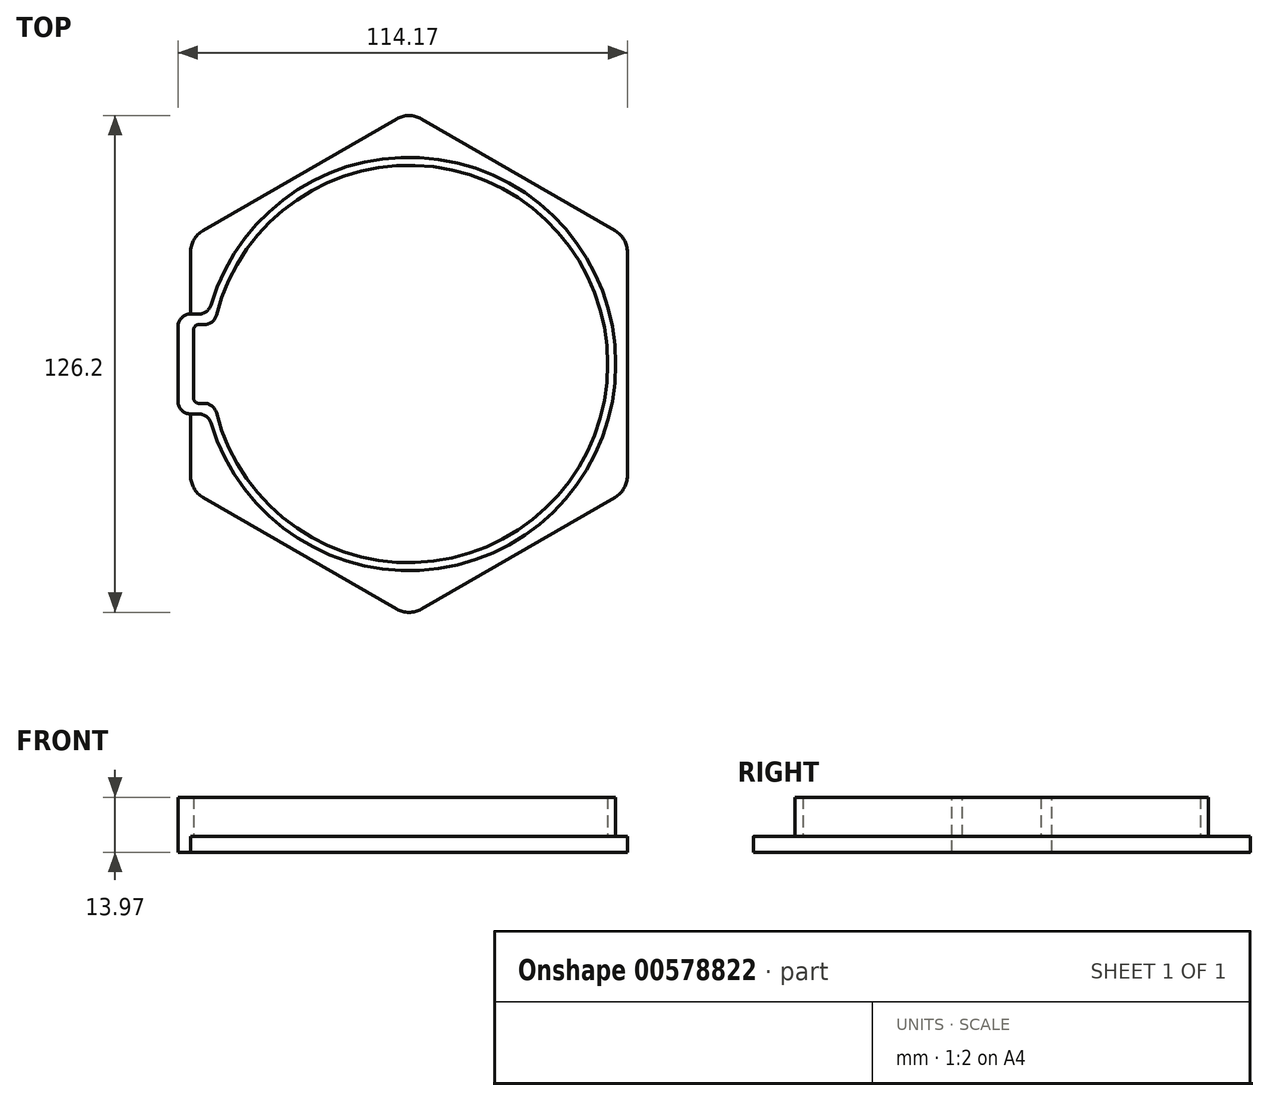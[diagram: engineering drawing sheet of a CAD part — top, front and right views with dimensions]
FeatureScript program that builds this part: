
annotation { "Feature Type Name" : "Feature", "Feature Type Description" : "" }
export const myFeature = defineFeature(function(context is Context, id is Id, definition is map)
    precondition{}
    {
        {
            var Q0;
            Q0=qCreatedBy(makeId("Top.planeOp"),FACE);
            var sketch = newSketch(context, id + "F0", { "sketchPlane" : qUnion([Q0])});
            skCircle(sketch, "E0.cCircle", {"center": v(0, 0) * mm, "radius": 64.08 * mm, "construction": true});
            skLineSegment(sketch, "E0.0", {"start": v(0, 64.08) * mm, "end": v(55.5, 32.04) * mm});
            skLineSegment(sketch, "E0.1", {"start": v(55.5, 32.04) * mm, "end": v(55.5, -32.04) * mm});
            skLineSegment(sketch, "E0.2", {"start": v(55.5, -32.04) * mm, "end": v(0, -64.08) * mm});
            skLineSegment(sketch, "E0.3", {"start": v(0, -64.08) * mm, "end": v(-55.5, -32.04) * mm});
            skLineSegment(sketch, "E0.4", {"start": v(-55.5, -32.04) * mm, "end": v(-55.5, 32.04) * mm});
            skLineSegment(sketch, "E0.5", {"start": v(-55.5, 32.04) * mm, "end": v(0, 64.08) * mm});
            skSolve(sketch);
        }
        {
            var Q0;
            Q0=makeQuery(id+"F0.imprint","IMPRINT",FACE,{"disambiguationData":[TD([[makeQuery(id+"F0.imprint","IMPRINT",EDGE,{"derivedFrom":sQuery(id+"F0.wireOp",EDGE,"E0.0")}),-1.0]])]});
            extrude(context, id + "F1", {"entities" : qUnion([Q0]), "depth" : 4 * mm, "offsetDistance" : 25.4 * mm});
        }
        {
            var Q0;
            Q0=makeQuery(id+"F1.opExtrude","CAP_FACE",FACE,{"disambiguationData":[OSD([sQuery(id+"F0.wireOp",EDGE,"E0.0"),sQuery(id+"F0.wireOp",EDGE,"E0.1"),sQuery(id+"F0.wireOp",EDGE,"E0.2"),sQuery(id+"F0.wireOp",EDGE,"E0.3"),sQuery(id+"F0.wireOp",EDGE,"E0.4"),sQuery(id+"F0.wireOp",EDGE,"E0.5")])],"isStart":false});
            var sketch = newSketch(context, id + "F2", { "sketchPlane" : qUnion([Q0])});
            skLineSegment(sketch, "E1.bottom", {"start": v(-55.5, -12.7) * mm, "end": v(-58.67, -12.7) * mm});
            skLineSegment(sketch, "E1.top", {"start": v(-55.5, 12.7) * mm, "end": v(-58.67, 12.7) * mm});
            skLineSegment(sketch, "E1.left", {"start": v(-55.5, -12.7) * mm, "end": v(-55.5, 12.7) * mm});
            skLineSegment(sketch, "E1.right", {"start": v(-58.67, -12.7) * mm, "end": v(-58.67, 12.7) * mm});
            skSolve(sketch);
        }
        {
            var Q0;
            Q0=makeQuery(id+"F2.imprint","IMPRINT",FACE,{"disambiguationData":[TD([[makeQuery(id+"F2.imprint","IMPRINT",EDGE,{"derivedFrom":sQuery(id+"F2.wireOp",EDGE,"E1.bottom")}),-1.0]])]});
            var Q1;
            Q1=makeQuery(id+"F1.opExtrude","CAP_FACE",FACE,{"disambiguationData":[OSD([sQuery(id+"F0.wireOp",EDGE,"E0.0"),sQuery(id+"F0.wireOp",EDGE,"E0.1"),sQuery(id+"F0.wireOp",EDGE,"E0.2"),sQuery(id+"F0.wireOp",EDGE,"E0.3"),sQuery(id+"F0.wireOp",EDGE,"E0.4"),sQuery(id+"F0.wireOp",EDGE,"E0.5")])],"isStart":true});
            extrude(context, id + "F3", {"entities" : qUnion([Q0]), "operationType" : NewBodyOperationType.ADD, "endBound" : BoundingType.UP_TO_SURFACE, "oppositeDirection" : true, "depth" : 25.4 * mm, "endBoundEntityFace" : qUnion([Q1]), "offsetDistance" : 25.4 * mm});
        }
        {
            var Q0;
            Q0=makeQuery(id+"F1.opExtrude","CAP_FACE",FACE,{"disambiguationData":[OSD([sQuery(id+"F0.wireOp",EDGE,"E0.0"),sQuery(id+"F0.wireOp",EDGE,"E0.1"),sQuery(id+"F0.wireOp",EDGE,"E0.2"),sQuery(id+"F0.wireOp",EDGE,"E0.3"),sQuery(id+"F0.wireOp",EDGE,"E0.4"),sQuery(id+"F0.wireOp",EDGE,"E0.5")])],"isStart":false});
            var sketch = newSketch(context, id + "F4", { "sketchPlane" : qUnion([Q0])});
            skArc(sketch, "E2", {"start": v(-49.48, -10) * mm, "mid": v(50.48, 0) * mm, "end": v(-49.48, 10) * mm});
            skArc(sketch, "E3", {"start": v(-50.96, -12.7) * mm, "mid": v(52.51, 0) * mm, "end": v(-50.96, 12.7) * mm});
            skLineSegment(sketch, "E4", {"start": v(0, 0) * mm, "end": v(-68.43, 0) * mm, "construction": true});
            skPoint(sketch, "E4.endSnap0", {"position": v(-55.5, 0) * mm});
            skLineSegment(sketch, "E5.bottom", {"start": v(-49.48, -10) * mm, "end": v(-54.7, -10) * mm});
            skLineSegment(sketch, "E5.top", {"start": v(-49.48, 10) * mm, "end": v(-54.7, 10) * mm});
            skLineSegment(sketch, "E5.right", {"start": v(-54.7, -10) * mm, "end": v(-54.7, 10) * mm});
            skLineSegment(sketch, "E6", {"start": v(-50.96, -12.7) * mm, "end": v(-58.67, -12.7) * mm});
            skLineSegment(sketch, "E7", {"start": v(-58.67, -12.7) * mm, "end": v(-58.67, 12.7) * mm});
            skLineSegment(sketch, "E8", {"start": v(-58.67, 12.7) * mm, "end": v(-50.96, 12.7) * mm});
            skSolve(sketch);
        }
        {
            var Q0;
            Q0=makeQuery(id+"F4.imprint","IMPRINT",FACE,{"disambiguationData":[TD([[makeQuery(id+"F4.imprint","IMPRINT",EDGE,{"derivedFrom":sQuery(id+"F4.wireOp",EDGE,"E2")}),-1.0]])]});
            extrude(context, id + "F5", {"entities" : qUnion([Q0]), "operationType" : NewBodyOperationType.ADD, "depth" : 9.98 * mm, "offsetDistance" : 25.4 * mm});
        }
        {
            var Q0;
            Q0=makeQuery(id+"F1.opExtrude","SWEPT_EDGE",EDGE,{"disambiguationData":[OSD([sQuery(id+"F0.wireOp",EDGE,"E0.3"),sQuery(id+"F0.wireOp",EDGE,"E0.4")])]});
            var Q1;
            Q1=makeQuery(id+"F1.opExtrude","SWEPT_EDGE",EDGE,{"disambiguationData":[OSD([sQuery(id+"F0.wireOp",EDGE,"E0.2"),sQuery(id+"F0.wireOp",EDGE,"E0.3")])]});
            var Q2;
            Q2=makeQuery(id+"F1.opExtrude","SWEPT_EDGE",EDGE,{"disambiguationData":[OSD([sQuery(id+"F0.wireOp",EDGE,"E0.1"),sQuery(id+"F0.wireOp",EDGE,"E0.2")])]});
            var Q3;
            Q3=makeQuery(id+"F1.opExtrude","SWEPT_EDGE",EDGE,{"disambiguationData":[OSD([sQuery(id+"F0.wireOp",EDGE,"E0.0"),sQuery(id+"F0.wireOp",EDGE,"E0.1")])]});
            var Q4;
            Q4=makeQuery(id+"F1.opExtrude","SWEPT_EDGE",EDGE,{"disambiguationData":[OSD([sQuery(id+"F0.wireOp",EDGE,"E0.0"),sQuery(id+"F0.wireOp",EDGE,"E0.5")])]});
            var Q5;
            Q5=makeQuery(id+"F1.opExtrude","SWEPT_EDGE",EDGE,{"disambiguationData":[OSD([sQuery(id+"F0.wireOp",EDGE,"E0.4"),sQuery(id+"F0.wireOp",EDGE,"E0.5")])]});
            fillet(context, id + "F6", {"entities" : qUnion([Q0, Q1, Q2, Q3, Q4, Q5]), "radius" : 6.35 * mm, "tangentPropagation" : true, "allowEdgeOverflow" : false});
        }
        {
            var Q0;
            Q0=makeQuery(id+"F5.opExtrude","SWEPT_EDGE",EDGE,{"disambiguationData":[OSD([sQuery(id+"F4.wireOp",EDGE,"E5.bottom"),sQuery(id+"F4.wireOp",EDGE,"E5.right")])]});
            var Q1;
            Q1=makeQuery(id+"F5.opExtrude","SWEPT_EDGE",EDGE,{"disambiguationData":[OSD([sQuery(id+"F4.wireOp",EDGE,"E5.top"),sQuery(id+"F4.wireOp",EDGE,"E5.right")])]});
            fillet(context, id + "F7", {"entities" : qUnion([Q0, Q1]), "radius" : 1.27 * mm, "tangentPropagation" : true, "allowEdgeOverflow" : false});
        }
        {
            var Q0;
            Q0=makeQuery(id+"F5.opExtrude","SWEPT_EDGE",EDGE,{"disambiguationData":[OSD([sQuery(id+"F4.wireOp",EDGE,"E2"),sQuery(id+"F4.wireOp",EDGE,"E5.bottom")])]});
            var Q1;
            Q1=makeQuery(id+"F5.opExtrude","SWEPT_EDGE",EDGE,{"disambiguationData":[OSD([sQuery(id+"F4.wireOp",EDGE,"E2"),sQuery(id+"F4.wireOp",EDGE,"E5.top")])]});
            var Q2;
            Q2=makeQuery(id+"F5.opExtrude","SWEPT_EDGE",EDGE,{"disambiguationData":[OSD([sQuery(id+"F4.wireOp",EDGE,"E3"),sQuery(id+"F4.wireOp",EDGE,"E8")])]});
            var Q3;
            Q3=makeQuery(id+"F5.boolean.opBoolean","MERGE",EDGE,{"derivedFrom":[makeQuery(id+"F3.opExtrude","SWEPT_EDGE",EDGE,{"disambiguationData":[OSD([sQuery(id+"F2.wireOp",EDGE,"E1.top"),sQuery(id+"F2.wireOp",EDGE,"E1.right")])]}),makeQuery(id+"F5.opExtrude","SWEPT_EDGE",EDGE,{"disambiguationData":[OSD([sQuery(id+"F4.wireOp",EDGE,"E7"),sQuery(id+"F4.wireOp",EDGE,"E8")])]})]});
            var Q4;
            Q4=makeQuery(id+"F5.boolean.opBoolean","MERGE",EDGE,{"derivedFrom":[makeQuery(id+"F3.opExtrude","SWEPT_EDGE",EDGE,{"disambiguationData":[OSD([sQuery(id+"F2.wireOp",EDGE,"E1.bottom"),sQuery(id+"F2.wireOp",EDGE,"E1.right")])]}),makeQuery(id+"F5.opExtrude","SWEPT_EDGE",EDGE,{"disambiguationData":[OSD([sQuery(id+"F4.wireOp",EDGE,"E6"),sQuery(id+"F4.wireOp",EDGE,"E7")])]})]});
            var Q5;
            Q5=makeQuery(id+"F5.opExtrude","SWEPT_EDGE",EDGE,{"disambiguationData":[OSD([sQuery(id+"F4.wireOp",EDGE,"E3"),sQuery(id+"F4.wireOp",EDGE,"E6")])]});
            fillet(context, id + "F8", {"entities" : qUnion([Q0, Q1, Q2, Q3, Q4, Q5]), "radius" : 3.17 * mm, "tangentPropagation" : true, "allowEdgeOverflow" : false});
        }
    });
